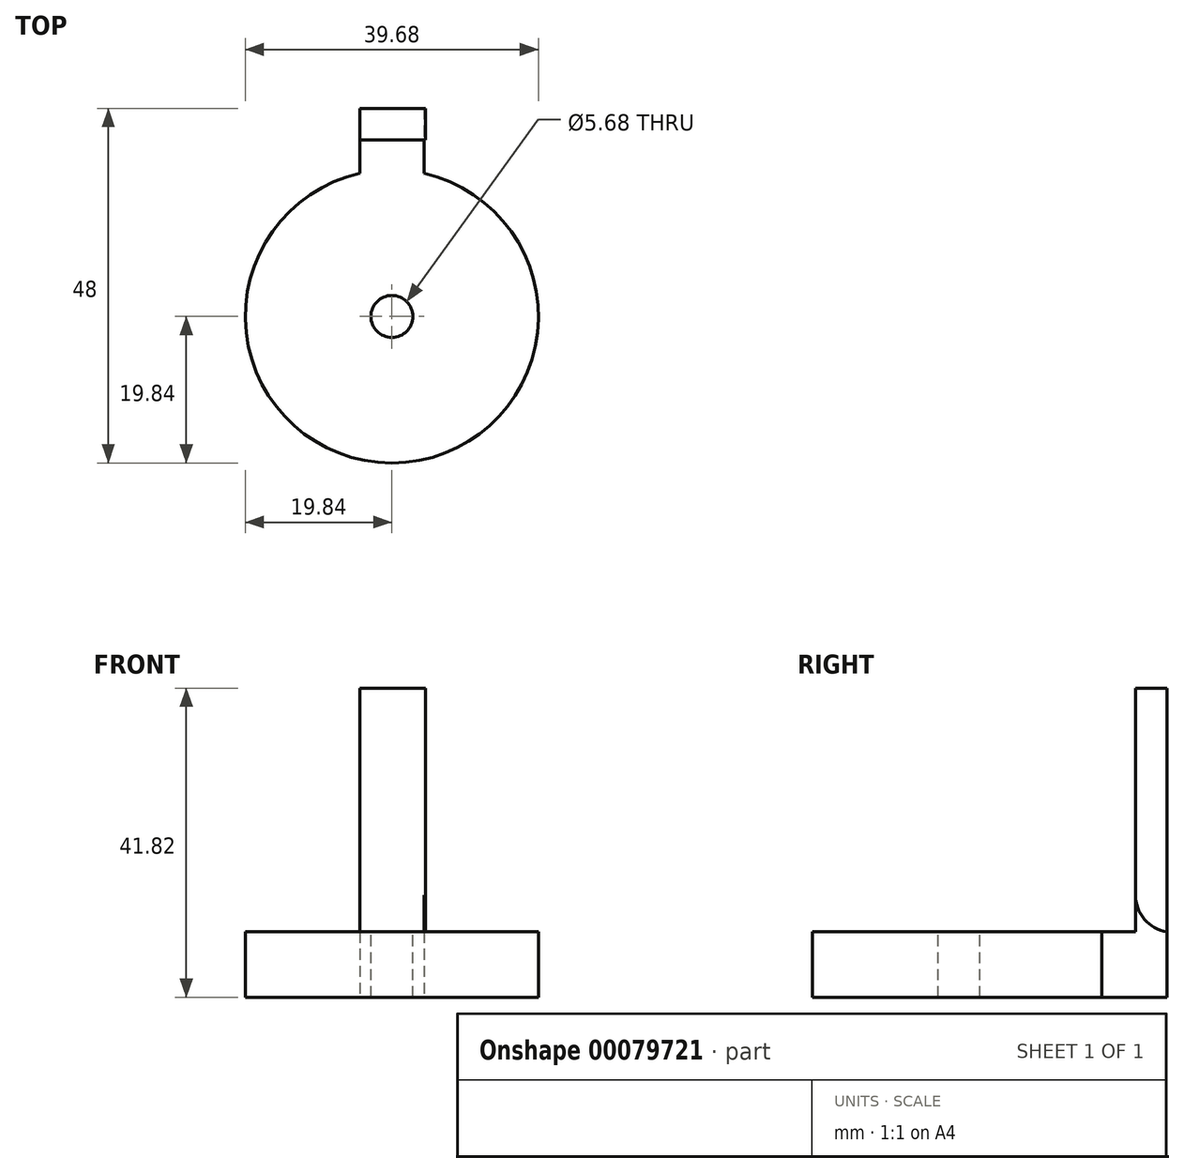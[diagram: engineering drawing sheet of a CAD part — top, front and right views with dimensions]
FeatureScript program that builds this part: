
annotation { "Feature Type Name" : "Feature", "Feature Type Description" : "" }
export const myFeature = defineFeature(function(context is Context, id is Id, definition is map)
    precondition{}
    {
        {
            var Q0;
            Q0=qCreatedBy(makeId("Top.planeOp"),FACE);
            var sketch = newSketch(context, id + "F0", { "sketchPlane" : qUnion([Q0])});
            skCircle(sketch, "E0", {"center": v(0, 0) * mm, "radius": 19.84 * mm});
            skSolve(sketch);
        }
        {
            var Q0;
            Q0 = qSketchRegion(id + "F0", true);
            extrude(context, id + "F1", {"entities" : qUnion([Q0]), "depth" : 8.86 * mm});
        }
        {
            var Q0;
            Q0=qCreatedBy(makeId("Top.planeOp"),FACE);
            var sketch = newSketch(context, id + "F2", { "sketchPlane" : qUnion([Q0])});
            skLineSegment(sketch, "E1.bottom", {"start": v(-4.33, 19.36) * mm, "end": v(4.33, 19.36) * mm});
            skLineSegment(sketch, "E1.top", {"start": v(-4.33, 28.16) * mm, "end": v(4.33, 28.16) * mm});
            skLineSegment(sketch, "E1.left", {"start": v(-4.33, 19.36) * mm, "end": v(-4.33, 28.16) * mm});
            skLineSegment(sketch, "E1.right", {"start": v(4.33, 19.36) * mm, "end": v(4.33, 28.16) * mm});
            skSolve(sketch);
        }
        {
            var Q0;
            Q0 = qSketchRegion(id + "F2", true);
            extrude(context, id + "F3", {"entities" : qUnion([Q0]), "operationType" : NewBodyOperationType.ADD, "depth" : 8.86 * mm});
        }
        {
            var Q0;
            Q0=makeQuery(id+"F3.boolean.opBoolean","MERGE",FACE,{"derivedFrom":[makeQuery(id+"F1.opExtrude","CAP_FACE",FACE,{"disambiguationData":[OSD([sQuery(id+"F0.wireOp",EDGE,"E0")])],"isStart":false}),makeQuery(id+"F3.opExtrude","CAP_FACE",FACE,{"disambiguationData":[OSD([sQuery(id+"F2.wireOp",EDGE,"E1.bottom"),sQuery(id+"F2.wireOp",EDGE,"E1.top"),sQuery(id+"F2.wireOp",EDGE,"E1.left"),sQuery(id+"F2.wireOp",EDGE,"E1.right")])],"isStart":false})]});
            var sketch = newSketch(context, id + "F4", { "sketchPlane" : qUnion([Q0])});
            skLineSegment(sketch, "E2.bottom", {"start": v(-4.33, 28.16) * mm, "end": v(4.53, 28.16) * mm});
            skLineSegment(sketch, "E2.top", {"start": v(-4.33, 23.9) * mm, "end": v(4.53, 23.9) * mm});
            skLineSegment(sketch, "E2.left", {"start": v(-4.33, 28.16) * mm, "end": v(-4.33, 23.9) * mm});
            skLineSegment(sketch, "E2.right", {"start": v(4.53, 28.16) * mm, "end": v(4.53, 23.9) * mm});
            skSolve(sketch);
        }
        {
            var Q0;
            Q0 = qSketchRegion(id + "F4", true);
            extrude(context, id + "F5", {"entities" : qUnion([Q0]), "operationType" : NewBodyOperationType.ADD, "depth" : 32.96 * mm});
        }
        {
            var Q0;
            Q0=makeQuery(id+"F3.boolean.opBoolean","MERGE",FACE,{"derivedFrom":[makeQuery(id+"F1.opExtrude","CAP_FACE",FACE,{"disambiguationData":[OSD([sQuery(id+"F0.wireOp",EDGE,"E0")])],"isStart":false}),makeQuery(id+"F3.opExtrude","CAP_FACE",FACE,{"disambiguationData":[OSD([sQuery(id+"F2.wireOp",EDGE,"E1.bottom"),sQuery(id+"F2.wireOp",EDGE,"E1.top"),sQuery(id+"F2.wireOp",EDGE,"E1.left"),sQuery(id+"F2.wireOp",EDGE,"E1.right")])],"isStart":false})]});
            var sketch = newSketch(context, id + "F6", { "sketchPlane" : qUnion([Q0])});
            skCircle(sketch, "E3", {"center": v(0, 0) * mm, "radius": 2.84 * mm});
            skSolve(sketch);
        }
        {
            var Q0;
            Q0 = qSketchRegion(id + "F6", true);
            var Q1;
            Q1=makeQuery(id+"F3.boolean.opBoolean","MERGE",FACE,{"derivedFrom":[makeQuery(id+"F1.opExtrude","CAP_FACE",FACE,{"disambiguationData":[OSD([sQuery(id+"F0.wireOp",EDGE,"E0")])],"isStart":true}),makeQuery(id+"F3.opExtrude","CAP_FACE",FACE,{"disambiguationData":[OSD([sQuery(id+"F2.wireOp",EDGE,"E1.bottom"),sQuery(id+"F2.wireOp",EDGE,"E1.top"),sQuery(id+"F2.wireOp",EDGE,"E1.left"),sQuery(id+"F2.wireOp",EDGE,"E1.right")])],"isStart":true})]});
            extrude(context, id + "F7", {"entities" : qUnion([Q0]), "operationType" : NewBodyOperationType.REMOVE, "endBound" : BoundingType.UP_TO_SURFACE, "oppositeDirection" : true, "endBoundEntityFace" : qUnion([Q1]), "depth" : 25 * mm});
        }
        {
            var Q0;
            {var subQ1=sQuery(id+"F2.wireOp",EDGE,"E1.left");var subQ3=sQuery(id+"F4.wireOp",EDGE,"E2.top");Q0=makeQuery(id+"F5.boolean.opBoolean","SPLIT",EDGE,{"disambiguationData":[TD([makeQuery(id+"F3.opExtrude","SWEPT_FACE",FACE,{"disambiguationData":[OSD([subQ1])]})])],"derivedFrom":makeQuery(id+"F5.opExtrude","CAP_EDGE",EDGE,{"disambiguationData":[OSD([subQ3])],"isStart":true})});}
            fillet(context, id + "F8", {"entities" : qUnion([Q0]), "radius" : 5 * mm, "tangentPropagation" : true, "allowEdgeOverflow" : false});
        }
    });
